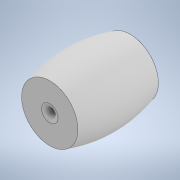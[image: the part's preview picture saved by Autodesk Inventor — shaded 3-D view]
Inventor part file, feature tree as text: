
AUTODESK INVENTOR PART (.ipt)
format: ipt  version: 2021 (Build 250183000, 183)  size: 131,584 bytes
history: native  units: in
note: dims shown in document units (in); Inventor stores cm internally (conversion verified against a paired STEP export)
features: revolve x1, fillet x1, sketch x1
ambient origin geometry x8: Origin, YZ Plane, XZ Plane, XY Plane, X Axis, Y Axis, Z Axis, Center Point
bodies: Solid1 (feature_tree)
feature tree (3):
  revolve  "Revolution1"  [1 undecoded]
  fillet  "Fillet1"  Radius=0.9843in
  sketch  "Sketch1"  dims[d0=0.5906in d1=0.2067in d2=0.9843in d3=0.0217in d4=90.0deg d5=0.0394in]
note: 1 required parameter value undecoded (feature->parameter linkage not recoverable at this tier; creation-order binding heuristic only, values carry confidence <= 0.55)
